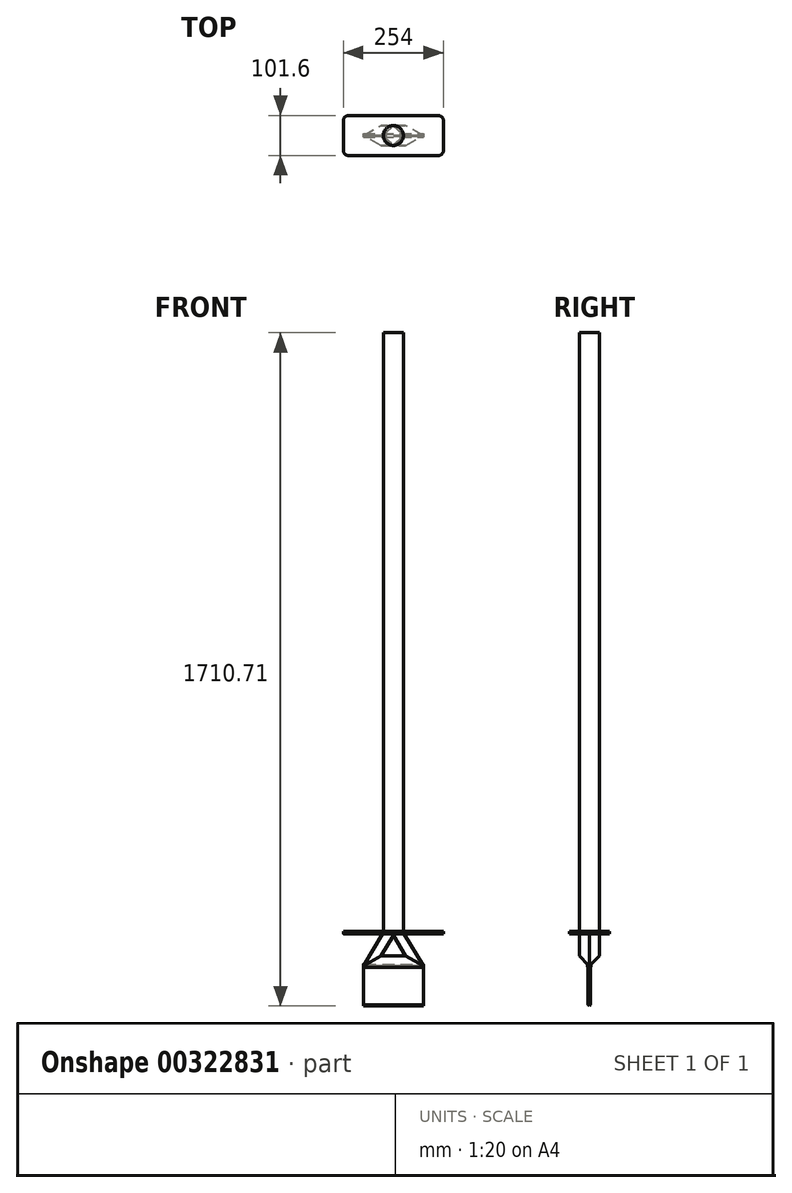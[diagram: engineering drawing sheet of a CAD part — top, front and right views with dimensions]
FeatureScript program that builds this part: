
annotation { "Feature Type Name" : "Feature", "Feature Type Description" : "" }
export const myFeature = defineFeature(function(context is Context, id is Id, definition is map)
    precondition{}
    {
        {
            var Q0;
            Q0=qCreatedBy(makeId("Front.planeOp"),FACE);
            var sketch = newSketch(context, id + "F0", { "sketchPlane" : qUnion([Q0])});
            skLineSegment(sketch, "E0.bottom", {"start": v(-25.4, 762) * mm, "end": v(25.4, 762) * mm});
            skLineSegment(sketch, "E0.top", {"start": v(-25.4, -762) * mm, "end": v(25.4, -762) * mm});
            skLineSegment(sketch, "E0.left", {"start": v(-25.4, 762) * mm, "end": v(-25.4, -762) * mm});
            skLineSegment(sketch, "E0.right", {"start": v(25.4, 762) * mm, "end": v(25.4, -762) * mm});
            skPoint(sketch, "E0.middle", {"position": v(0, 0) * mm});
            skPoint(sketch, "E1.middle", {"position": v(0, -762) * mm});
            skLineSegment(sketch, "E2.bottom", {"start": v(76.2, -948.7) * mm, "end": v(-76.2, -948.7) * mm});
            skLineSegment(sketch, "E2.top", {"start": v(76.2, -847.1) * mm, "end": v(-76.2, -847.1) * mm});
            skLineSegment(sketch, "E2.left", {"start": v(76.2, -948.7) * mm, "end": v(76.2, -847.1) * mm});
            skLineSegment(sketch, "E2.right", {"start": v(-76.2, -948.7) * mm, "end": v(-76.2, -847.1) * mm});
            skPoint(sketch, "E2.middle", {"position": v(0, -897.9) * mm});
            skLineSegment(sketch, "E3", {"start": v(-25.4, -762) * mm, "end": v(-76.2, -847.1) * mm});
            skLineSegment(sketch, "E4", {"start": v(76.2, -847.1) * mm, "end": v(25.4, -762) * mm});
            skLineSegment(sketch, "E5.bottom", {"start": v(127, -765.18) * mm, "end": v(-127, -765.18) * mm});
            skLineSegment(sketch, "E5.top", {"start": v(127, -758.83) * mm, "end": v(-127, -758.83) * mm});
            skLineSegment(sketch, "E5.left", {"start": v(127, -765.18) * mm, "end": v(127, -758.83) * mm});
            skLineSegment(sketch, "E5.right", {"start": v(-127, -765.18) * mm, "end": v(-127, -758.83) * mm});
            skPoint(sketch, "E6.middle", {"position": v(0, -847.1) * mm});
            skSolve(sketch);
        }
        {
            var Q0;
            {var subQ0=sQuery(id+"F0.wireOp",EDGE,"E0.bottom");Q0=makeQuery(id+"F0.imprint","IMPRINT",FACE,{"disambiguationData":[TD([[makeQuery(id+"F0.imprint","IMPRINT",EDGE,{"derivedFrom":subQ0}),-1.0]])]});}
            extrude(context, id + "F1", {"entities" : qUnion([Q0]), "endBound" : BoundingType.SYMMETRIC, "depth" : 50.8 * mm});
        }
        {
            var Q0;
            Q0=makeQuery(id+"F1.opExtrude","CAP_EDGE",EDGE,{"disambiguationData":[OSD([sQuery(id+"F0.wireOp",EDGE,"E0.left")])],"isStart":false});
            var Q1;
            Q1=makeQuery(id+"F1.opExtrude","CAP_EDGE",EDGE,{"disambiguationData":[OSD([sQuery(id+"F0.wireOp",EDGE,"E0.right")])],"isStart":false});
            var Q2;
            Q2=makeQuery(id+"F1.opExtrude","CAP_EDGE",EDGE,{"disambiguationData":[OSD([sQuery(id+"F0.wireOp",EDGE,"E0.right")])],"isStart":true});
            var Q3;
            Q3=makeQuery(id+"F1.opExtrude","CAP_EDGE",EDGE,{"disambiguationData":[OSD([sQuery(id+"F0.wireOp",EDGE,"E0.left")])],"isStart":true});
            fillet(context, id + "F2", {"entities" : qUnion([Q0, Q1, Q2, Q3]), "radius" : 25.4 * mm, "tangentPropagation" : true, "allowEdgeOverflow" : false});
        }
        {
            var Q0;
            Q0=makeQuery(id+"F0.imprint","IMPRINT",FACE,{"disambiguationData":[TD([[makeQuery(id+"F0.imprint","IMPRINT",EDGE,{"derivedFrom":sQuery(id+"F0.wireOp",EDGE,"E2.bottom")}),-1.0]])]});
            extrude(context, id + "F3", {"entities" : qUnion([Q0]), "endBound" : BoundingType.SYMMETRIC, "depth" : 6.35 * mm});
        }
        {
            var Q0;
            {var subQ0=sQuery(id+"F0.wireOp",EDGE,"E2.top");Q0=makeQuery(id+"F0.imprint","IMPRINT",FACE,{"disambiguationData":[TD([[makeQuery(id+"F0.imprint","IMPRINT",EDGE,{"derivedFrom":subQ0}),-1.0]])]});}
            var Q1;
            {var subQ0=sQuery(id+"F0.wireOp",EDGE,"E5.bottom");var subQ1=sQuery(id+"F0.wireOp",EDGE,"E3");var subQ2=makeQuery(id+"F0.imprint","INTERSECT",VERTEX,{"derivedFrom":[subQ1,subQ0]});Q1=makeQuery(id+"F0.imprint","IMPRINT",FACE,{"disambiguationData":[TD([[makeQuery(id+"F0.imprint","IMPRINT",EDGE,{"disambiguationData":[TD([[subQ2,-1.0]])],"derivedFrom":subQ1}),1.0]])]});}
            extrude(context, id + "F4", {"entities" : qUnion([Q0, Q1]), "endBound" : BoundingType.SYMMETRIC, "depth" : 50.8 * mm});
        }
        {
            var Q0;
            Q0=makeQuery(id+"F4.opExtrude","CAP_EDGE",EDGE,{"disambiguationData":[OSD([sQuery(id+"F0.wireOp",EDGE,"E2.top")])],"isStart":true});
            var Q1;
            Q1=makeQuery(id+"F4.opExtrude","CAP_EDGE",EDGE,{"disambiguationData":[OSD([sQuery(id+"F0.wireOp",EDGE,"E3")])],"isStart":true});
            var Q2;
            Q2=makeQuery(id+"F4.opExtrude","CAP_EDGE",EDGE,{"disambiguationData":[OSD([sQuery(id+"F0.wireOp",EDGE,"E4")])],"isStart":true});
            var Q3;
            Q3=makeQuery(id+"F4.opExtrude","CAP_EDGE",EDGE,{"disambiguationData":[OSD([sQuery(id+"F0.wireOp",EDGE,"E4")])],"isStart":false});
            var Q4;
            Q4=makeQuery(id+"F4.opExtrude","CAP_EDGE",EDGE,{"disambiguationData":[OSD([sQuery(id+"F0.wireOp",EDGE,"E3")])],"isStart":false});
            var Q5;
            Q5=makeQuery(id+"F4.opExtrude","CAP_EDGE",EDGE,{"disambiguationData":[OSD([sQuery(id+"F0.wireOp",EDGE,"E2.top")])],"isStart":false});
            chamfer(context, id + "F5", {"entities" : qUnion([Q0, Q1, Q2, Q3, Q4, Q5]), "width" : 25.4 * mm, "tangentPropagation" : true});
        }
        {
            var Q0;
            Q0=makeQuery(id+"F3.opExtrude","CAP_EDGE",EDGE,{"disambiguationData":[OSD([sQuery(id+"F0.wireOp",EDGE,"E2.bottom")])],"isStart":true});
            var Q1;
            Q1=makeQuery(id+"F3.opExtrude","CAP_EDGE",EDGE,{"disambiguationData":[OSD([sQuery(id+"F0.wireOp",EDGE,"E2.bottom")])],"isStart":false});
            chamfer(context, id + "F6", {"entities" : qUnion([Q0, Q1]), "width" : 3.17 * mm, "tangentPropagation" : true});
        }
        {
            var Q0;
            {var subQ0=sQuery(id+"F0.wireOp",EDGE,"E5.left");Q0=makeQuery(id+"F0.imprint","IMPRINT",FACE,{"disambiguationData":[TD([[makeQuery(id+"F0.imprint","IMPRINT",EDGE,{"derivedFrom":subQ0}),1.0]])]});}
            var Q1;
            {var subQ0=sQuery(id+"F0.wireOp",EDGE,"E5.right");Q1=makeQuery(id+"F0.imprint","IMPRINT",FACE,{"disambiguationData":[TD([[makeQuery(id+"F0.imprint","IMPRINT",EDGE,{"derivedFrom":subQ0}),-1.0]])]});}
            var Q2;
            {var subQ0=sQuery(id+"F0.wireOp",EDGE,"E0.top");Q2=makeQuery(id+"F0.imprint","IMPRINT",FACE,{"disambiguationData":[TD([[makeQuery(id+"F0.imprint","IMPRINT",EDGE,{"derivedFrom":subQ0}),1.0]])]});}
            var Q3;
            {var subQ0=sQuery(id+"F0.wireOp",EDGE,"E0.top");Q3=makeQuery(id+"F0.imprint","IMPRINT",FACE,{"disambiguationData":[TD([[makeQuery(id+"F0.imprint","IMPRINT",EDGE,{"derivedFrom":subQ0}),-1.0]])]});}
            extrude(context, id + "F7", {"entities" : qUnion([Q0, Q1, Q2, Q3]), "endBound" : BoundingType.SYMMETRIC, "depth" : 101.6 * mm});
        }
        {
            var Q0;
            Q0=makeQuery(id+"F7.opExtrude","CAP_EDGE",EDGE,{"disambiguationData":[OSD([sQuery(id+"F0.wireOp",EDGE,"E5.left")])],"isStart":true});
            var Q1;
            Q1=makeQuery(id+"F7.opExtrude","CAP_EDGE",EDGE,{"disambiguationData":[OSD([sQuery(id+"F0.wireOp",EDGE,"E5.left")])],"isStart":false});
            var Q2;
            Q2=makeQuery(id+"F7.opExtrude","CAP_EDGE",EDGE,{"disambiguationData":[OSD([sQuery(id+"F0.wireOp",EDGE,"E5.right")])],"isStart":false});
            var Q3;
            Q3=makeQuery(id+"F7.opExtrude","CAP_EDGE",EDGE,{"disambiguationData":[OSD([sQuery(id+"F0.wireOp",EDGE,"E5.right")])],"isStart":true});
            fillet(context, id + "F8", {"entities" : qUnion([Q0, Q1, Q2, Q3]), "radius" : 12.7 * mm, "tangentPropagation" : true, "allowEdgeOverflow" : false});
        }
        {
            var Q0;
            Q0=makeQuery(id+"F3.opExtrude","CAP_EDGE",EDGE,{"disambiguationData":[OSD([sQuery(id+"F0.wireOp",EDGE,"E2.top")])],"isStart":true});
            var Q1;
            Q1=makeQuery(id+"F3.opExtrude","CAP_EDGE",EDGE,{"disambiguationData":[OSD([sQuery(id+"F0.wireOp",EDGE,"E2.top")])],"isStart":false});
            chamfer(context, id + "F9", {"entities" : qUnion([Q0, Q1]), "width" : 3.17 * mm, "tangentPropagation" : true});
        }
        {
            var Q0;
            {var subQ0=sQuery(id+"F0.wireOp",EDGE,"E2.top");Q0=makeQuery(id+"F9.opChamfer","BLEND_FACE",FACE,{"disambiguationData":[OSD([subQ0]),TDD([makeQuery(id+"F3.opExtrude","CAP_EDGE",EDGE,{"disambiguationData":[OSD([subQ0])],"isStart":false})])]});}
            var Q1;
            Q1=sQuery(id+"F0.wireOp",EDGE,"E2.top");
            var Q2;
            Q2=sQuery(id+"F0.wireOp",EDGE,"E2.top");
            revolve(context, id + "F10", {"entities" : qUnion([Q0]), "surfaceEntities" : qUnion([Q1]), "axis" : qUnion([Q2]), "revolveType" : RevolveType.SYMMETRIC, "angle" : 360 * degree});
        }
    });
